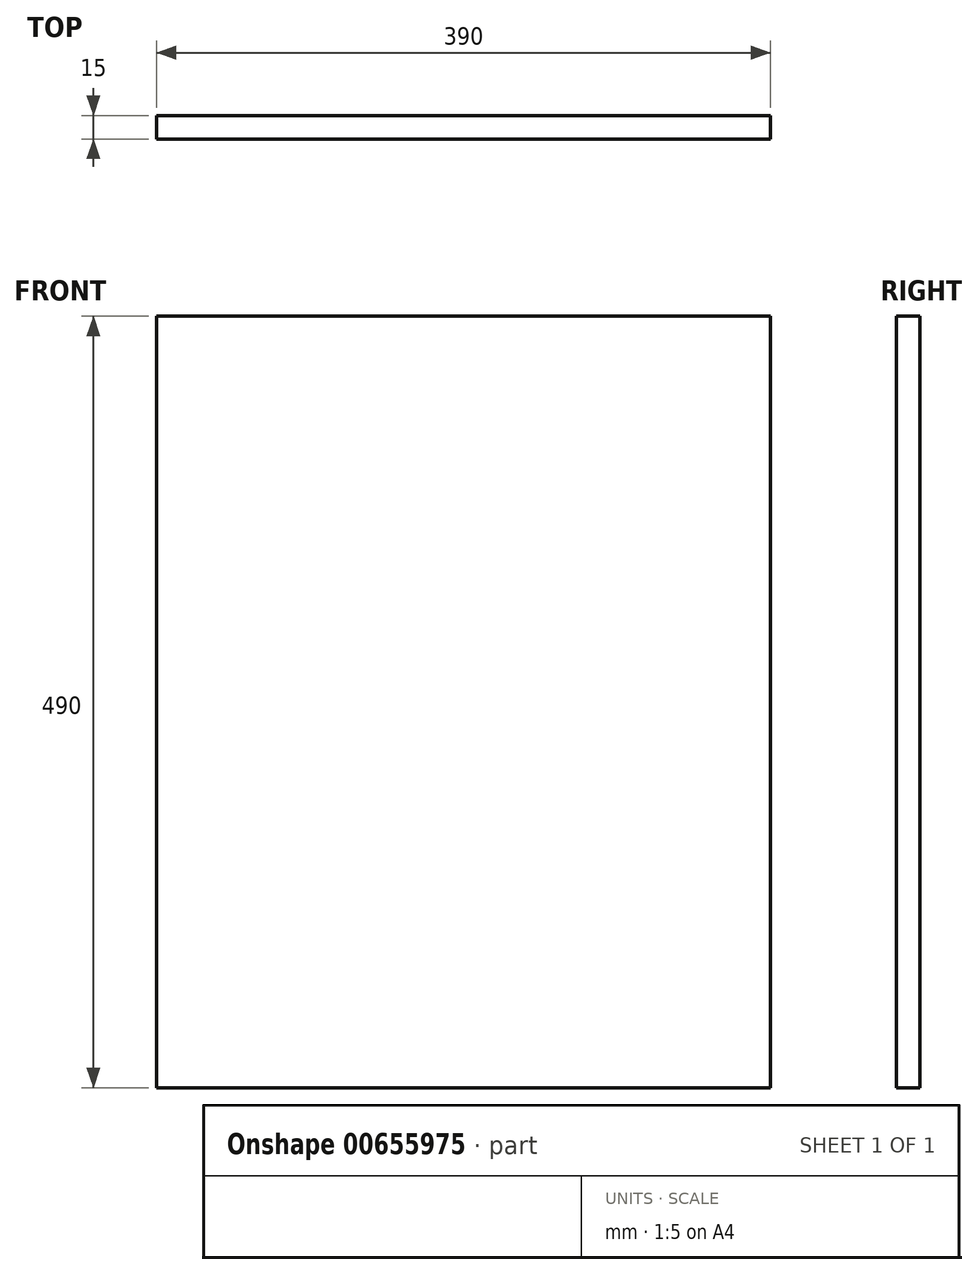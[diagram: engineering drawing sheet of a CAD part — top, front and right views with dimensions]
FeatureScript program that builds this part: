
annotation { "Feature Type Name" : "Feature", "Feature Type Description" : "" }
export const myFeature = defineFeature(function(context is Context, id is Id, definition is map)
    precondition{}
    {
        {
            var Q0;
            Q0=qCreatedBy(makeId("Front.planeOp"),FACE);
            var sketch = newSketch(context, id + "F0", { "sketchPlane" : qUnion([Q0])});
            skLineSegment(sketch, "E0.bottom", {"start": v(0, 0) * mm, "end": v(390, 0) * mm});
            skLineSegment(sketch, "E0.top", {"start": v(0, 490) * mm, "end": v(390, 490) * mm});
            skLineSegment(sketch, "E0.left", {"start": v(0, 0) * mm, "end": v(0, 490) * mm});
            skLineSegment(sketch, "E0.right", {"start": v(390, 0) * mm, "end": v(390, 490) * mm});
            skSolve(sketch);
        }
        {
            var Q0;
            Q0=makeQuery(id+"F0.imprint","IMPRINT",FACE,{"disambiguationData":[TD([[makeQuery(id+"F0.imprint","IMPRINT",EDGE,{"derivedFrom":sQuery(id+"F0.wireOp",EDGE,"E0.bottom")}),1.0]])]});
            extrude(context, id + "F1", {"entities" : qUnion([Q0]), "depth" : 15 * mm, "offsetDistance" : 25.4 * mm});
        }
    });
